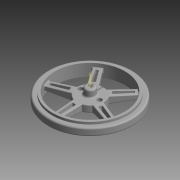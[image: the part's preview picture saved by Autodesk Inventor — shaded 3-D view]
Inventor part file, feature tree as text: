
AUTODESK INVENTOR PART (.ipt)
format: ipt  version: 2014 (Build 180170000, 170)  size: 1,454,080 bytes
history: native  units: mm
features: sketch x11, extrude x10, fillet x6, pattern_circular x2, plane x1, other x1, mirror x1, revolve x1, projected_geometry x1
ambient origin geometry x8: Origin, YZ Plane, XZ Plane, XY Plane, X Axis, Y Axis, Z Axis, Center Point
bodies: Volumenkörper1 (feature_tree)
feature tree (34):
  extrude  "Extrusion1"  Depth=8.0mm TaperAngle=0.0deg
  plane  "Arbeitsebene2"
  other  "Arbeitsachse1"
  extrude  "Extrusion2"  Depth=1.5mm TaperAngle=0.0deg
  extrude  "Extrusion3"  Depth=1.7mm TaperAngle=0.0deg
  mirror  "Spiegeln2"
  extrude  "Extrusion11"  Depth=3.0mm
  extrude  "Extrusion7"  Depth=1.7mm TaperAngle=0.0deg
  extrude  "Extrusion8"  Depth=1.7mm
  pattern_circular  "Runde Anordnung2"  Count=5 Angle=360.0deg
  extrude  "Extrusion9"  Depth=1.7mm
  pattern_circular  "Runde Anordnung3"  [2 undecoded]
  extrude  "Extrusion6"  Depth=1.0mm TaperAngle=360.0deg
  sketch  "Skizze15"  dims[d54=17.75mm d55=1.7mm]
  revolve  "Umdrehung1"
  fillet  "Rundung11"  Radius=6.35mm
  fillet  "Rundung12"  Radius=1.0mm
  fillet  "Rundung13"  Radius=1.7mm
  fillet  "Rundung14"  Radius=6.5mm
  extrude  "Extrusion12"  Depth=1.0mm TaperAngle=0.0deg
  extrude  "Extrusion10"  Depth=1.0mm
  fillet  "Rundung15"  Radius=1.0mm
  fillet  "Rundung16"  [1 undecoded]
  sketch  "Skizze1"  dims[d0=56.0mm d1=8.0mm d2=0.0mm]
  sketch  "Skizze2"  dims[d3=50.0mm d4=1.5mm d5=0.0mm]
  sketch  "Skizze3"  dims[d6=1.7mm d7=1.7mm d8=0.0mm]
  sketch  "Skizze6"  dims[d27=3.0mm d28=3.0mm]
  sketch  "Skizze7"  dims[d29=12.7mm d31=1.7mm d32=0.0mm]
  sketch  "Skizze9"  dims[d41=1.7mm d42=0.0mm d45=1.7mm]
  sketch  "Skizze10"  dims[d46=2.3mm]
  sketch  "Skizze11"  dims[d48=11.0mm]
  sketch  "Skizze13"  dims[d49=1.7mm d50=0.0mm d51=50.0mm d52=360.0deg]
  projected_geometry  "Projizierte Kontur1"
  sketch  "Skizze16"  dims[d57=1.7mm d58=1.7mm d59=0.0mm d60=50.0mm d61=360.0deg d63=6.35mm d64=1.0mm d65=1.7mm d66=0.0mm d68=6.5mm d69=4.7mm d70=0.0mm d78=1.0mm d79=1.0mm d80=90.0deg d83=0.5mm d90=0.5mm d91=0.5mm d98=0.5mm d99=1.0mm d100=5.0mm d101=5.0mm d102=5.0mm d103=0.0mm d104=1.0mm d105=1.0mm d106=3.0mm d107=1.0mm d108=10.0mm]
note: 3 required parameter values undecoded (feature->parameter linkage not recoverable at this tier; creation-order binding heuristic only, values carry confidence <= 0.55)
